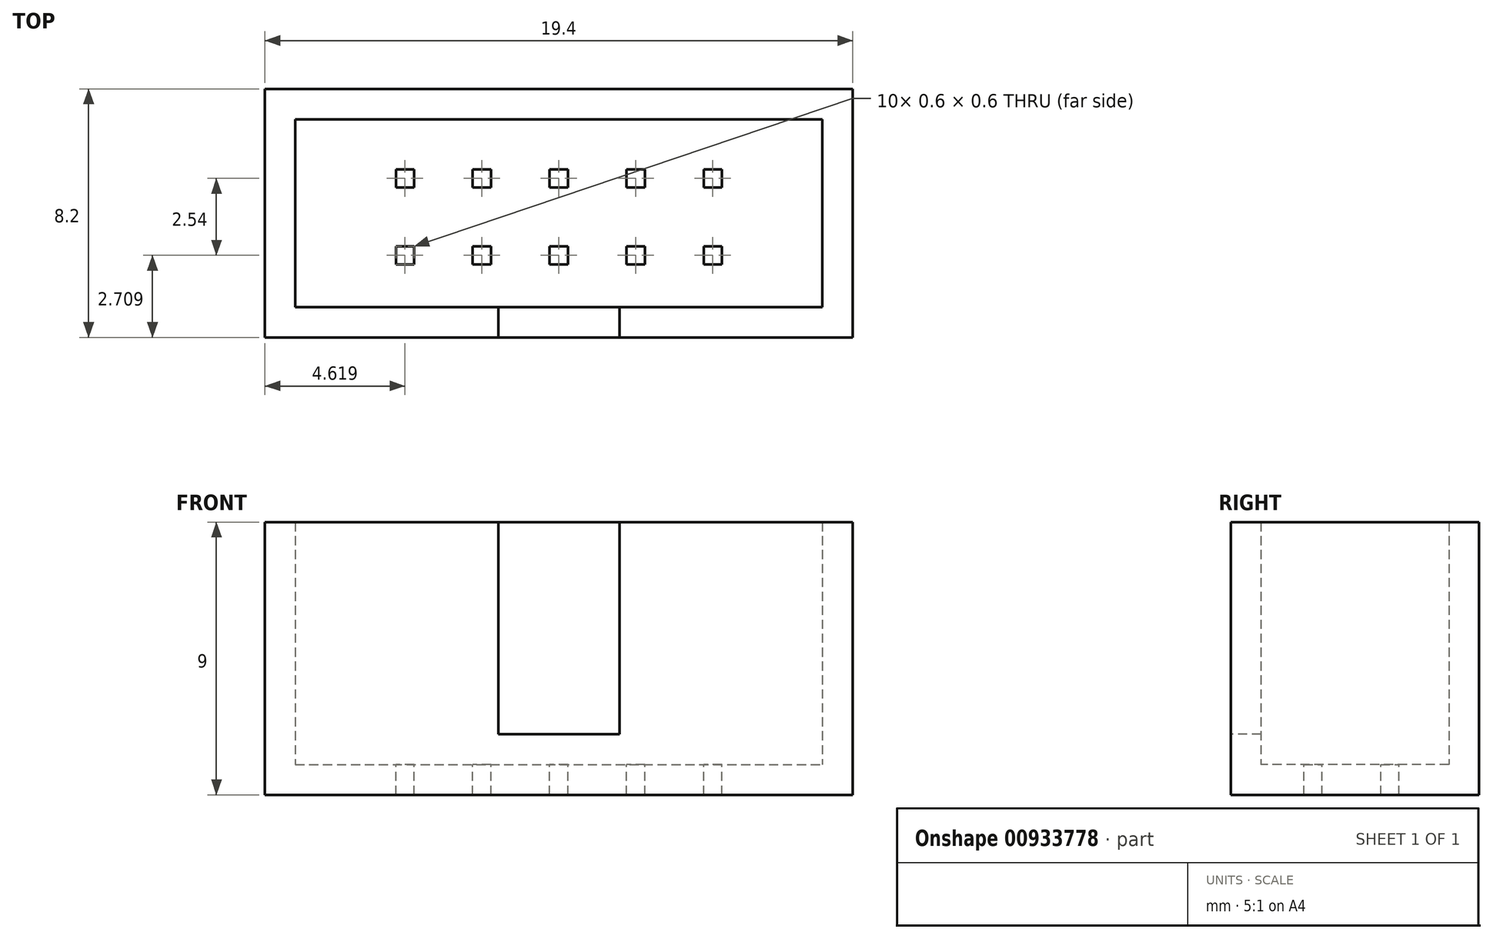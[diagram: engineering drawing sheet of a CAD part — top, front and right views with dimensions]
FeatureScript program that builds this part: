
annotation { "Feature Type Name" : "Feature", "Feature Type Description" : "" }
export const myFeature = defineFeature(function(context is Context, id is Id, definition is map)
    precondition{}
    {
        {
            var Q0;
            Q0=qCreatedBy(makeId("Top.planeOp"),FACE);
            var sketch = newSketch(context, id + "F0", { "sketchPlane" : qUnion([Q0])});
            skLineSegment(sketch, "E0.bottom", {"start": v(-7.42, 16.45) * mm, "end": v(9.98, 16.45) * mm});
            skLineSegment(sketch, "E0.top", {"start": v(-7.42, 10.25) * mm, "end": v(9.98, 10.25) * mm});
            skLineSegment(sketch, "E0.left", {"start": v(-7.42, 16.45) * mm, "end": v(-7.42, 10.25) * mm});
            skLineSegment(sketch, "E0.right", {"start": v(9.98, 16.45) * mm, "end": v(9.98, 10.25) * mm});
            skLineSegment(sketch, "E1.bottom", {"start": v(-8.42, 17.45) * mm, "end": v(10.98, 17.45) * mm});
            skLineSegment(sketch, "E1.top", {"start": v(-8.42, 9.25) * mm, "end": v(10.98, 9.25) * mm});
            skLineSegment(sketch, "E1.left", {"start": v(-8.42, 17.45) * mm, "end": v(-8.42, 9.25) * mm});
            skLineSegment(sketch, "E1.right", {"start": v(10.98, 17.45) * mm, "end": v(10.98, 9.25) * mm});
            skSolve(sketch);
        }
        {
            var Q0;
            Q0=makeQuery(id+"F0.imprint","IMPRINT",FACE,{"disambiguationData":[TD([[makeQuery(id+"F0.imprint","IMPRINT",EDGE,{"derivedFrom":sQuery(id+"F0.wireOp",EDGE,"E0.bottom")}),-1.0]])]});
            extrude(context, id + "F1", {"entities" : qUnion([Q0]), "depth" : 1 * mm, "offsetDistance" : 25 * mm});
        }
        {
            var Q0;
            Q0=makeQuery(id+"F0.imprint","IMPRINT",FACE,{"disambiguationData":[TD([[makeQuery(id+"F0.imprint","IMPRINT",EDGE,{"derivedFrom":sQuery(id+"F0.wireOp",EDGE,"E0.bottom")}),1.0]])]});
            extrude(context, id + "F2", {"entities" : qUnion([Q0]), "operationType" : NewBodyOperationType.ADD, "depth" : 9 * mm, "offsetDistance" : 25 * mm});
        }
        {
            var Q0;
            Q0=makeQuery(id+"F2.opExtrude","SWEPT_FACE",FACE,{"disambiguationData":[OSD([sQuery(id+"F0.wireOp",EDGE,"E1.top")])]});
            var sketch = newSketch(context, id + "F3", { "sketchPlane" : qUnion([Q0])});
            skLineSegment(sketch, "E2", {"start": v(1.28, 9) * mm, "end": v(1.28, 0) * mm, "construction": true});
            skLineSegment(sketch, "E3", {"start": v(-0.72, 2) * mm, "end": v(3.28, 2) * mm});
            skLineSegment(sketch, "E4", {"start": v(-0.72, 2) * mm, "end": v(-0.72, 9) * mm});
            skLineSegment(sketch, "E5", {"start": v(3.28, 2) * mm, "end": v(3.28, 9) * mm});
            skSolve(sketch);
        }
        {
            var Q0;
            Q0=makeQuery(id+"F3.imprint","IMPRINT",FACE,{"disambiguationData":[TD([[makeQuery(id+"F3.imprint","IMPRINT",EDGE,{"derivedFrom":sQuery(id+"F3.wireOp",EDGE,"E3")}),1.0]])]});
            extrude(context, id + "F4", {"entities" : qUnion([Q0]), "operationType" : NewBodyOperationType.REMOVE, "oppositeDirection" : true, "depth" : 2 * mm, "offsetDistance" : 25 * mm});
        }
        {
            var Q0;
            Q0=makeQuery(id+"F1.opExtrude","CAP_FACE",FACE,{"disambiguationData":[OSD([sQuery(id+"F0.wireOp",EDGE,"E0.bottom"),sQuery(id+"F0.wireOp",EDGE,"E0.top"),sQuery(id+"F0.wireOp",EDGE,"E0.left"),sQuery(id+"F0.wireOp",EDGE,"E0.right")])],"isStart":false});
            var sketch = newSketch(context, id + "F5", { "sketchPlane" : qUnion([Q0])});
            skLineSegment(sketch, "E6.bottom", {"start": v(-3.5, 14.2) * mm, "end": v(-4.1, 14.2) * mm});
            skLineSegment(sketch, "E6.top", {"start": v(-3.5, 14.8) * mm, "end": v(-4.1, 14.8) * mm});
            skLineSegment(sketch, "E6.left", {"start": v(-3.5, 14.2) * mm, "end": v(-3.5, 14.8) * mm});
            skLineSegment(sketch, "E6.right", {"start": v(-4.1, 14.2) * mm, "end": v(-4.1, 14.8) * mm});
            skPoint(sketch, "E6.middle", {"position": v(-3.8, 14.5) * mm});
            skLineSegment(sketch, "E7.0.1.0", {"start": v(-4.1, 11.66) * mm, "end": v(-4.1, 12.26) * mm});
            skLineSegment(sketch, "E7.0.1.1", {"start": v(-3.5, 11.66) * mm, "end": v(-4.1, 11.66) * mm});
            skLineSegment(sketch, "E7.0.1.2", {"start": v(-3.5, 11.66) * mm, "end": v(-3.5, 12.26) * mm});
            skPoint(sketch, "E7.0.1.3", {"position": v(-3.8, 11.96) * mm});
            skLineSegment(sketch, "E7.0.1.4", {"start": v(-3.5, 12.26) * mm, "end": v(-4.1, 12.26) * mm});
            skLineSegment(sketch, "E7.1.0.0", {"start": v(-1.56, 14.2) * mm, "end": v(-1.56, 14.8) * mm});
            skLineSegment(sketch, "E7.1.0.1", {"start": v(-0.96, 14.2) * mm, "end": v(-1.56, 14.2) * mm});
            skLineSegment(sketch, "E7.1.0.2", {"start": v(-0.96, 14.2) * mm, "end": v(-0.96, 14.8) * mm});
            skPoint(sketch, "E7.1.0.3", {"position": v(-1.26, 14.5) * mm});
            skLineSegment(sketch, "E7.1.0.4", {"start": v(-0.96, 14.8) * mm, "end": v(-1.56, 14.8) * mm});
            skLineSegment(sketch, "E7.1.1.0", {"start": v(-1.56, 11.66) * mm, "end": v(-1.56, 12.26) * mm});
            skLineSegment(sketch, "E7.1.1.1", {"start": v(-0.96, 11.66) * mm, "end": v(-1.56, 11.66) * mm});
            skLineSegment(sketch, "E7.1.1.2", {"start": v(-0.96, 11.66) * mm, "end": v(-0.96, 12.26) * mm});
            skPoint(sketch, "E7.1.1.3", {"position": v(-1.26, 11.96) * mm});
            skLineSegment(sketch, "E7.1.1.4", {"start": v(-0.96, 12.26) * mm, "end": v(-1.56, 12.26) * mm});
            skLineSegment(sketch, "E7.2.0.0", {"start": v(0.98, 14.2) * mm, "end": v(0.98, 14.8) * mm});
            skLineSegment(sketch, "E7.2.0.1", {"start": v(1.58, 14.2) * mm, "end": v(0.98, 14.2) * mm});
            skLineSegment(sketch, "E7.2.0.2", {"start": v(1.58, 14.2) * mm, "end": v(1.58, 14.8) * mm});
            skPoint(sketch, "E7.2.0.3", {"position": v(1.28, 14.5) * mm});
            skLineSegment(sketch, "E7.2.0.4", {"start": v(1.58, 14.8) * mm, "end": v(0.98, 14.8) * mm});
            skLineSegment(sketch, "E7.2.1.0", {"start": v(0.98, 11.66) * mm, "end": v(0.98, 12.26) * mm});
            skLineSegment(sketch, "E7.2.1.1", {"start": v(1.58, 11.66) * mm, "end": v(0.98, 11.66) * mm});
            skLineSegment(sketch, "E7.2.1.2", {"start": v(1.58, 11.66) * mm, "end": v(1.58, 12.26) * mm});
            skPoint(sketch, "E7.2.1.3", {"position": v(1.28, 11.96) * mm});
            skLineSegment(sketch, "E7.2.1.4", {"start": v(1.58, 12.26) * mm, "end": v(0.98, 12.26) * mm});
            skLineSegment(sketch, "E7.3.0.0", {"start": v(3.52, 14.2) * mm, "end": v(3.52, 14.8) * mm});
            skLineSegment(sketch, "E7.3.0.1", {"start": v(4.12, 14.2) * mm, "end": v(3.52, 14.2) * mm});
            skLineSegment(sketch, "E7.3.0.2", {"start": v(4.12, 14.2) * mm, "end": v(4.12, 14.8) * mm});
            skPoint(sketch, "E7.3.0.3", {"position": v(3.82, 14.5) * mm});
            skLineSegment(sketch, "E7.3.0.4", {"start": v(4.12, 14.8) * mm, "end": v(3.52, 14.8) * mm});
            skLineSegment(sketch, "E7.3.1.0", {"start": v(3.52, 11.66) * mm, "end": v(3.52, 12.26) * mm});
            skLineSegment(sketch, "E7.3.1.1", {"start": v(4.12, 11.66) * mm, "end": v(3.52, 11.66) * mm});
            skLineSegment(sketch, "E7.3.1.2", {"start": v(4.12, 11.66) * mm, "end": v(4.12, 12.26) * mm});
            skPoint(sketch, "E7.3.1.3", {"position": v(3.82, 11.96) * mm});
            skLineSegment(sketch, "E7.3.1.4", {"start": v(4.12, 12.26) * mm, "end": v(3.52, 12.26) * mm});
            skLineSegment(sketch, "E7.4.0.0", {"start": v(6.06, 14.2) * mm, "end": v(6.06, 14.8) * mm});
            skLineSegment(sketch, "E7.4.0.1", {"start": v(6.66, 14.2) * mm, "end": v(6.06, 14.2) * mm});
            skLineSegment(sketch, "E7.4.0.2", {"start": v(6.66, 14.2) * mm, "end": v(6.66, 14.8) * mm});
            skPoint(sketch, "E7.4.0.3", {"position": v(6.36, 14.5) * mm});
            skLineSegment(sketch, "E7.4.0.4", {"start": v(6.66, 14.8) * mm, "end": v(6.06, 14.8) * mm});
            skLineSegment(sketch, "E7.4.1.0", {"start": v(6.06, 11.66) * mm, "end": v(6.06, 12.26) * mm});
            skLineSegment(sketch, "E7.4.1.1", {"start": v(6.66, 11.66) * mm, "end": v(6.06, 11.66) * mm});
            skLineSegment(sketch, "E7.4.1.2", {"start": v(6.66, 11.66) * mm, "end": v(6.66, 12.26) * mm});
            skPoint(sketch, "E7.4.1.3", {"position": v(6.36, 11.96) * mm});
            skLineSegment(sketch, "E7.4.1.4", {"start": v(6.66, 12.26) * mm, "end": v(6.06, 12.26) * mm});
            skLineSegment(sketch, "E7.direction1", {"start": v(-4.1, 14.2) * mm, "end": v(-1.56, 14.2) * mm, "construction": true});
            skLineSegment(sketch, "E7.direction2", {"start": v(-4.1, 14.2) * mm, "end": v(-4.1, 11.66) * mm, "construction": true});
            skLineSegment(sketch, "E8", {"start": v(1.28, 16.45) * mm, "end": v(1.28, 10.25) * mm, "construction": true});
            skSolve(sketch);
        }
        {
            var Q0;
            Q0=makeQuery(id+"F5.imprint","IMPRINT",FACE,{"disambiguationData":[TD([[makeQuery(id+"F5.imprint","IMPRINT",EDGE,{"derivedFrom":sQuery(id+"F5.wireOp",EDGE,"E7.0.1.0")}),-1.0]])]});
            var Q1;
            Q1=makeQuery(id+"F5.imprint","IMPRINT",FACE,{"disambiguationData":[TD([[makeQuery(id+"F5.imprint","IMPRINT",EDGE,{"derivedFrom":sQuery(id+"F5.wireOp",EDGE,"E6.bottom")}),-1.0]])]});
            var Q2;
            Q2=makeQuery(id+"F5.imprint","IMPRINT",FACE,{"disambiguationData":[TD([[makeQuery(id+"F5.imprint","IMPRINT",EDGE,{"derivedFrom":sQuery(id+"F5.wireOp",EDGE,"E7.1.0.0")}),-1.0]])]});
            var Q3;
            Q3=makeQuery(id+"F5.imprint","IMPRINT",FACE,{"disambiguationData":[TD([[makeQuery(id+"F5.imprint","IMPRINT",EDGE,{"derivedFrom":sQuery(id+"F5.wireOp",EDGE,"E7.1.1.0")}),-1.0]])]});
            var Q4;
            Q4=makeQuery(id+"F5.imprint","IMPRINT",FACE,{"disambiguationData":[TD([[makeQuery(id+"F5.imprint","IMPRINT",EDGE,{"derivedFrom":sQuery(id+"F5.wireOp",EDGE,"E7.2.1.0")}),-1.0]])]});
            var Q5;
            Q5=makeQuery(id+"F5.imprint","IMPRINT",FACE,{"disambiguationData":[TD([[makeQuery(id+"F5.imprint","IMPRINT",EDGE,{"derivedFrom":sQuery(id+"F5.wireOp",EDGE,"E7.2.0.0")}),-1.0]])]});
            var Q6;
            Q6=makeQuery(id+"F5.imprint","IMPRINT",FACE,{"disambiguationData":[TD([[makeQuery(id+"F5.imprint","IMPRINT",EDGE,{"derivedFrom":sQuery(id+"F5.wireOp",EDGE,"E7.3.1.0")}),-1.0]])]});
            var Q7;
            Q7=makeQuery(id+"F5.imprint","IMPRINT",FACE,{"disambiguationData":[TD([[makeQuery(id+"F5.imprint","IMPRINT",EDGE,{"derivedFrom":sQuery(id+"F5.wireOp",EDGE,"E7.3.0.0")}),-1.0]])]});
            var Q8;
            Q8=makeQuery(id+"F5.imprint","IMPRINT",FACE,{"disambiguationData":[TD([[makeQuery(id+"F5.imprint","IMPRINT",EDGE,{"derivedFrom":sQuery(id+"F5.wireOp",EDGE,"E7.4.0.0")}),-1.0]])]});
            var Q9;
            Q9=makeQuery(id+"F5.imprint","IMPRINT",FACE,{"disambiguationData":[TD([[makeQuery(id+"F5.imprint","IMPRINT",EDGE,{"derivedFrom":sQuery(id+"F5.wireOp",EDGE,"E7.4.1.0")}),-1.0]])]});
            extrude(context, id + "F6", {"entities" : qUnion([Q0, Q1, Q2, Q3, Q4, Q5, Q6, Q7, Q8, Q9]), "operationType" : NewBodyOperationType.REMOVE, "oppositeDirection" : true, "depth" : 25 * mm, "offsetDistance" : 25 * mm});
        }
    });
